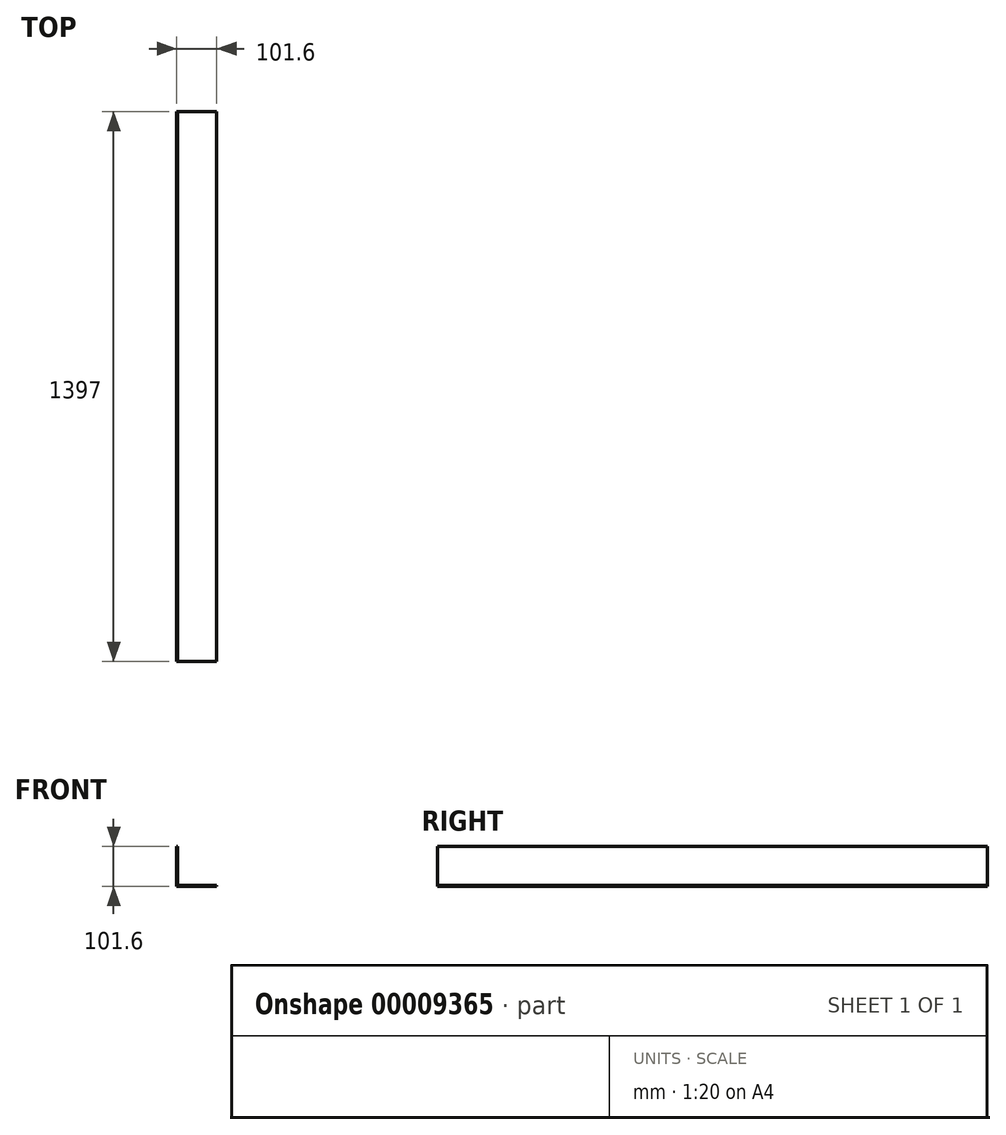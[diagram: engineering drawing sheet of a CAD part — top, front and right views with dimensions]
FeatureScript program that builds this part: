
annotation { "Feature Type Name" : "Feature", "Feature Type Description" : "" }
export const myFeature = defineFeature(function(context is Context, id is Id, definition is map)
    precondition{}
    {
        {
            var Q0;
            Q0=qCreatedBy(makeId("Front.planeOp"),FACE);
            var sketch = newSketch(context, id + "F0", { "sketchPlane" : qUnion([Q0])});
            skLineSegment(sketch, "E0", {"start": v(-46.9, 56.92) * mm, "end": v(-46.9, -44.68) * mm});
            skLineSegment(sketch, "E1", {"start": v(-46.9, -44.68) * mm, "end": v(54.7, -44.68) * mm});
            skLineSegment(sketch, "E2", {"start": v(54.7, -44.68) * mm, "end": v(54.7, -41.92) * mm});
            skLineSegment(sketch, "E3", {"start": v(54.7, -41.92) * mm, "end": v(-44.14, -41.92) * mm});
            skLineSegment(sketch, "E4", {"start": v(-44.14, -41.92) * mm, "end": v(-44.14, 56.92) * mm});
            skLineSegment(sketch, "E5", {"start": v(-44.14, 56.92) * mm, "end": v(-46.9, 56.92) * mm});
            skSolve(sketch);
        }
        {
            var Q0;
            Q0=makeQuery(id+"F0.imprint","IMPRINT",FACE,{"disambiguationData":[TD([[makeQuery(id+"F0.imprint","IMPRINT",EDGE,{"derivedFrom":sQuery(id+"F0.wireOp",EDGE,"E0")}),1.0]])]});
            extrude(context, id + "F1", {"entities" : qUnion([Q0]), "depth" : 1397 * mm});
        }
    });
